FCSTD DOCUMENT  (FreeCAD 0.19R0.19.2)
Label: v0_05
License: All rights reserved
LicenseURL: http://en.wikipedia.org/wiki/All_rights_reserved
objects: Sketcher::SketchObject×1
note: 1 computed .brp shape members not serialized (recipe doc carries the construction recipe); baked Part::Feature solids carry a one-line shape summary decoded from their .brp

FEATURE [Sketcher::SketchObject] Sketch
  FullyConstrained = true
  sketch-geometry (35):
    g0: LineSegment StartX=0 StartY=0 StartZ=0 EndX=111.35 EndY=0 EndZ=0
    g1: Circle CenterX=111.35 CenterY=-15.15 CenterZ=0 NormalX=0 NormalY=0 NormalZ=1 AngleXU=0 Radius=3.25
    g2: LineSegment StartX=111.35 StartY=0 StartZ=0 EndX=144.4 EndY=0 EndZ=0
    g3: LineSegment StartX=144.9 StartY=-7.5 StartZ=0 EndX=151.9 EndY=-7.5 EndZ=0
    g4: LineSegment StartX=111.35 StartY=0 StartZ=0 EndX=98.1 EndY=0 EndZ=0
    g5: Circle CenterX=81.35 CenterY=-6.2 CenterZ=0 NormalX=0 NormalY=0 NormalZ=1 AngleXU=0 Radius=1.3
    g6: Circle CenterX=61.25 CenterY=-6.2 CenterZ=0 NormalX=0 NormalY=0 NormalZ=1 AngleXU=0 Radius=1.3
    g7: LineSegment StartX=111.35 StartY=0 StartZ=0 EndX=81.35 EndY=0 EndZ=0
    g8: LineSegment StartX=144.4 StartY=0 StartZ=0 EndX=144.4 EndY=-7 EndZ=0
    g9: ArcOfCircle CenterX=144.9 CenterY=-7 CenterZ=0 NormalX=0 NormalY=0 NormalZ=1 AngleXU=0 Radius=0.5 StartAngle=3.14159 EndAngle=4.71239
    g10: Circle CenterX=81.35 CenterY=-14.2 CenterZ=0 NormalX=0 NormalY=0 NormalZ=1 AngleXU=0 Radius=1.3
    g11: Circle CenterX=61.25 CenterY=-14.2 CenterZ=0 NormalX=0 NormalY=0 NormalZ=1 AngleXU=0 Radius=1.3
    g12: LineSegment StartX=61.25 StartY=-15.5 StartZ=0 EndX=61.25 EndY=-20.4 EndZ=0
    g13: LineSegment StartX=111.35 StartY=-15.15 StartZ=0 EndX=104.85 EndY=-15.15 EndZ=0
    g14: LineSegment StartX=61.25 StartY=-20.4 StartZ=0 EndX=104.85 EndY=-20.4 EndZ=0
    g15: LineSegment StartX=109.725 StartY=-21.65 StartZ=0 EndX=111.35 EndY=-21.65 EndZ=0
    g16-g20: Circle x5 (B-spline internal-alignment scaffolding for g21; pole/knot coordinates omitted)
    g21: BSplineCurve PolesCount=5 KnotsCount=3 Degree=3 IsPeriodic=0
    g22: GeomPoint X=104.85 Y=-20.4 Z=0
    g23: GeomPoint X=108.1 Y=-21.0125 Z=0
    g24: GeomPoint X=111.35 Y=-21.65 Z=0
    g25: LineSegment StartX=111.35 StartY=-21.65 StartZ=0 EndX=112.975 EndY=-21.65 EndZ=0
    g26-g30: Circle x5 (B-spline internal-alignment scaffolding for g31; pole/knot coordinates omitted)
    g31: BSplineCurve PolesCount=5 KnotsCount=3 Degree=3 IsPeriodic=0
    g32: GeomPoint X=111.35 Y=-21.65 Z=0
    g33: GeomPoint X=114.6 Y=-21.0125 Z=0
    g34: GeomPoint X=117.85 Y=-20.4 Z=0
  constraints (61):
    c: Coincident(g0,g-1)
    c: PointOnObject(g0,g-1)
    c: Distance(g0) = 111.35
    c: Radius(g1) = 3.25
    c: Block(g1)
    c: Horizontal(g2)
    c: Distance(g2) = 33.05
    c: Coincident(g2,g0)
    c: Horizontal(g4)
    c: Distance(g4) = 13.25
    c: Coincident(g4,g0)
    c: Horizontal(g7)
    c: Distance(g7) = 30
    c: Coincident(g7,g0)
    c: Block(g5)
    c: Block(g6)
    c: Vertical(g8)
    c: Distance(g8) = 7
    c: Coincident(g8,g2)
    c: Coincident(g9,g8)
    c: Coincident(g9,g3)
    c: Block(g3)
    c: Block(g9)
    c: Block(g10)
    c: Block(g11)
    c: Vertical(g12)
    c: Distance(g12) = 4.9
    c: Block(g12)
    c: Horizontal(g13)
    c: Coincident(g13,g1)
    c: Distance(g13) = 6.5
    c: Horizontal(g14)
    c: Coincident(g14,g12)
    c: Block(g14)
    c: Horizontal(g15)
    c: Distance(g15) = 1.625
    c: Coincident(g21,g14)
    c: Weight(g16) = 1
    c: Equal(g16,g17)
    c: Equal(g16,g18)
    c: Equal(g16,g19)
    c: Coincident(g19,g15)
    c: Equal(g16,g20)
    c: InternalAlignment(g16-g20 -> g21) x5
    c: InternalAlignment(g22,g21)
    c: InternalAlignment(g23,g21)
    c: InternalAlignment(g24,g21)
    c: Horizontal(g25)
    c: Distance(g25) = 1.625
    c: Weight(g26) = 1
    c: Equal(g26,g27)
    c: Coincident(g27,g25)
    c: Equal(g26,g28)
    c: Equal(g26,g29)
    c: Equal(g26,g30)
    c: InternalAlignment(g26-g30 -> g31) x5
    c: InternalAlignment(g32,g31)
    c: InternalAlignment(g33,g31)
    c: InternalAlignment(g34,g31)
    c: Block(g31)
    c: Block(g21)
